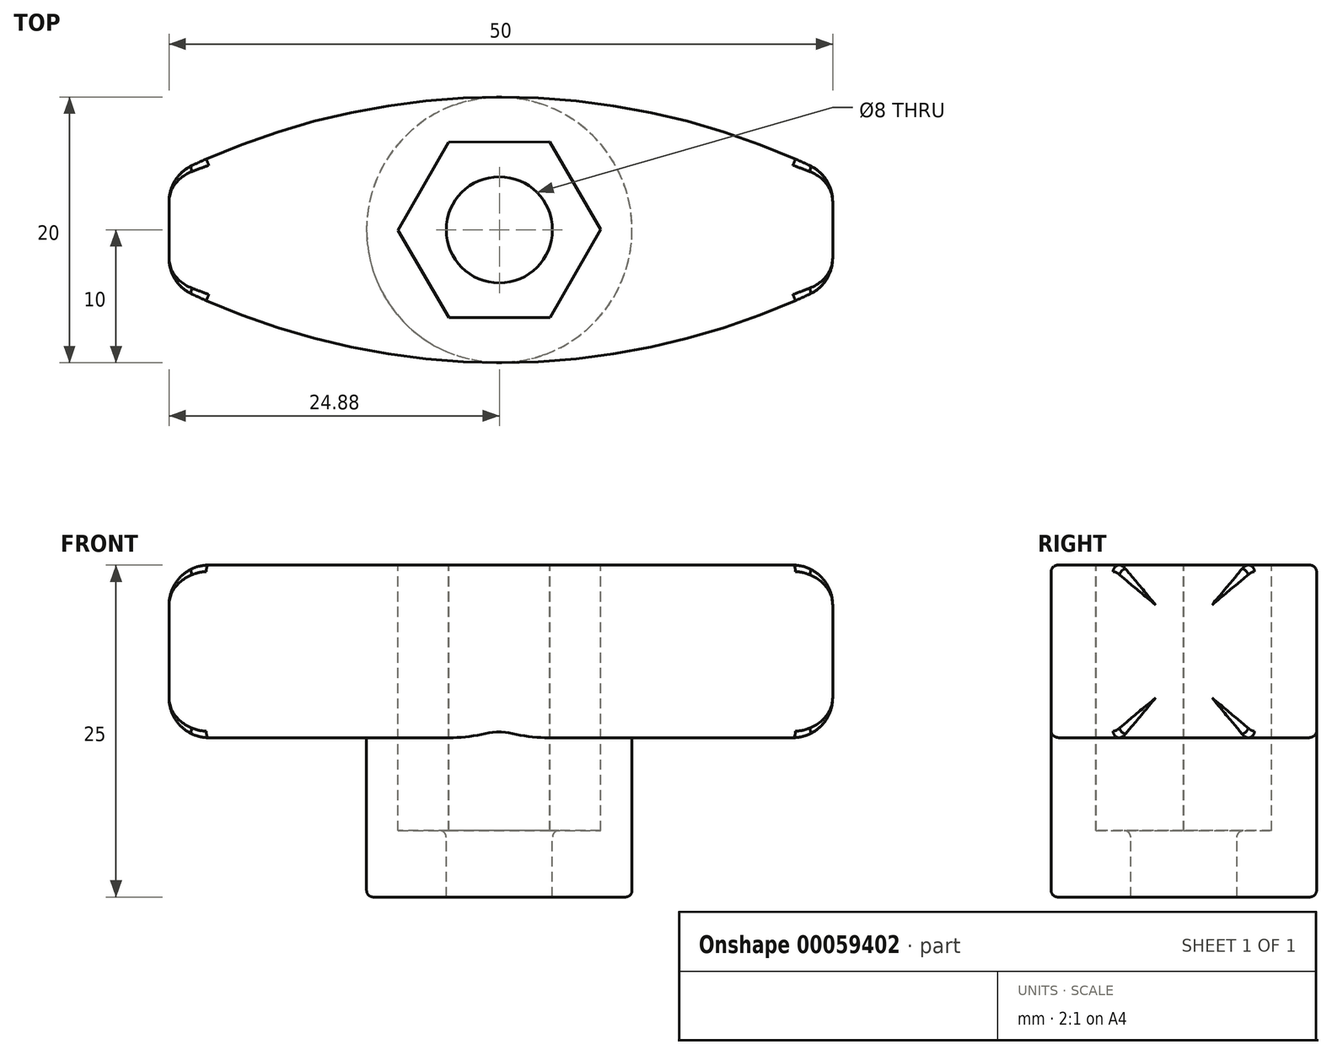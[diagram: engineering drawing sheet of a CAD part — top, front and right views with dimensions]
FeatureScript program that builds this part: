
annotation { "Feature Type Name" : "Feature", "Feature Type Description" : "" }
export const myFeature = defineFeature(function(context is Context, id is Id, definition is map)
    precondition{}
    {
        {
            var Q0;
            Q0=qCreatedBy(makeId("Top.planeOp"),FACE);
            var sketch = newSketch(context, id + "F0", { "sketchPlane" : qUnion([Q0])});
            skArc(sketch, "E0", {"start": v(25.12, 4) * mm, "mid": v(0.12, 10) * mm, "end": v(-24.88, 4) * mm});
            skArc(sketch, "E1.MirrorCS", {"start": v(25.12, -4) * mm, "mid": v(0.12, -10) * mm, "end": v(-24.88, -4) * mm});
            skLineSegment(sketch, "E2", {"start": v(-24.88, -4) * mm, "end": v(-24.88, 4) * mm});
            skLineSegment(sketch, "E3", {"start": v(25.12, 4) * mm, "end": v(25.12, -4) * mm});
            skSolve(sketch);
        }
        {
            var Q0;
            Q0 = qSketchRegion(id + "F0", true);
            extrude(context, id + "F1", {"entities" : qUnion([Q0]), "depth" : 13 * mm});
        }
        {
            var Q0;
            Q0=makeQuery(id+"F1.opExtrude","CAP_FACE",FACE,{"disambiguationData":[OSD([sQuery(id+"F0.wireOp",EDGE,"E0"),sQuery(id+"F0.wireOp",EDGE,"E1.MirrorCS"),sQuery(id+"F0.wireOp",EDGE,"E2"),sQuery(id+"F0.wireOp",EDGE,"E3")])],"isStart":true});
            var sketch = newSketch(context, id + "F2", { "sketchPlane" : qUnion([Q0])});
            skCircle(sketch, "E4", {"center": v(0, 0) * mm, "radius": 10 * mm});
            skSolve(sketch);
        }
        {
            var Q0;
            Q0 = qSketchRegion(id + "F2", true);
            extrude(context, id + "F3", {"entities" : qUnion([Q0]), "operationType" : NewBodyOperationType.ADD, "depth" : 12 * mm});
        }
        {
            var Q0;
            Q0=makeQuery(id+"F1.opExtrude","CAP_FACE",FACE,{"disambiguationData":[OSD([sQuery(id+"F0.wireOp",EDGE,"E0"),sQuery(id+"F0.wireOp",EDGE,"E1.MirrorCS"),sQuery(id+"F0.wireOp",EDGE,"E2"),sQuery(id+"F0.wireOp",EDGE,"E3")])],"isStart":false});
            var sketch = newSketch(context, id + "F4", { "sketchPlane" : qUnion([Q0])});
            skCircle(sketch, "E5", {"center": v(0, 0) * mm, "radius": 4 * mm});
            skSolve(sketch);
        }
        {
            var Q0;
            Q0=makeQuery(id+"F4.imprint","IMPRINT",FACE,{"disambiguationData":[TD([[makeQuery(id+"F4.imprint","IMPRINT",EDGE,{"derivedFrom":sQuery(id+"F4.wireOp",EDGE,"E5")}),1.0]])]});
            extrude(context, id + "F5", {"entities" : qUnion([Q0]), "operationType" : NewBodyOperationType.REMOVE, "oppositeDirection" : true, "depth" : 25 * mm});
        }
        {
            var Q0;
            Q0=makeQuery(id+"F1.opExtrude","CAP_FACE",FACE,{"disambiguationData":[OSD([sQuery(id+"F0.wireOp",EDGE,"E0"),sQuery(id+"F0.wireOp",EDGE,"E1.MirrorCS"),sQuery(id+"F0.wireOp",EDGE,"E2"),sQuery(id+"F0.wireOp",EDGE,"E3")])],"isStart":false});
            var sketch = newSketch(context, id + "F6", { "sketchPlane" : qUnion([Q0])});
            skCircle(sketch, "E6.cCircle", {"center": v(0, 0) * mm, "radius": 6.61 * mm, "construction": true});
            skLineSegment(sketch, "E6.0", {"start": v(-7.63, -0.02) * mm, "end": v(-3.83, 6.6) * mm});
            skLineSegment(sketch, "E6.1", {"start": v(-3.83, 6.6) * mm, "end": v(3.8, 6.62) * mm});
            skLineSegment(sketch, "E6.2", {"start": v(3.8, 6.62) * mm, "end": v(7.63, 0.02) * mm});
            skLineSegment(sketch, "E6.3", {"start": v(7.63, 0.02) * mm, "end": v(3.83, -6.6) * mm});
            skLineSegment(sketch, "E6.4", {"start": v(3.83, -6.6) * mm, "end": v(-3.8, -6.62) * mm});
            skLineSegment(sketch, "E6.5", {"start": v(-3.8, -6.62) * mm, "end": v(-7.63, -0.02) * mm});
            skPoint(sketch, "E6.0.midPoint", {"position": v(-5.73, 3.3) * mm});
            skSolve(sketch);
        }
        {
            var Q0;
            Q0 = qSketchRegion(id + "F6", true);
            extrude(context, id + "F7", {"entities" : qUnion([Q0]), "operationType" : NewBodyOperationType.REMOVE, "oppositeDirection" : true, "depth" : 20 * mm});
        }
        {
            var Q0;
            Q0=makeQuery(id+"F3.opExtrude","CAP_EDGE",EDGE,{"disambiguationData":[OSD([sQuery(id+"F2.wireOp",EDGE,"E4")])],"isStart":false});
            var Q1;
            Q1=makeQuery(id+"F5.boolean.opBoolean","COPY",EDGE,{"derivedFrom":makeQuery(id+"F5.opExtrude","CAP_EDGE",EDGE,{"disambiguationData":[OSD([sQuery(id+"F4.wireOp",EDGE,"E5")])],"isStart":false})});
            var Q2;
            Q2=makeQuery(id+"F7.boolean.opBoolean","INTERSECT",EDGE,{"derivedFrom":[makeQuery(id+"F5.boolean.opBoolean","COPY",FACE,{"derivedFrom":makeQuery(id+"F5.opExtrude","SWEPT_FACE",FACE,{"disambiguationData":[OSD([sQuery(id+"F4.wireOp",EDGE,"E5")])]})}),makeQuery(id+"F7.opExtrude","CAP_FACE",FACE,{"disambiguationData":[OSD([sQuery(id+"F6.wireOp",EDGE,"E6.0"),sQuery(id+"F6.wireOp",EDGE,"E6.1"),sQuery(id+"F6.wireOp",EDGE,"E6.2"),sQuery(id+"F6.wireOp",EDGE,"E6.3"),sQuery(id+"F6.wireOp",EDGE,"E6.4"),sQuery(id+"F6.wireOp",EDGE,"E6.5")])],"isStart":false})]});
            var Q3;
            Q3=makeQuery(id+"F7.boolean.opBoolean","COPY",EDGE,{"derivedFrom":makeQuery(id+"F7.opExtrude","CAP_EDGE",EDGE,{"disambiguationData":[OSD([sQuery(id+"F6.wireOp",EDGE,"E6.0")])],"isStart":true})});
            var Q4;
            Q4=makeQuery(id+"F7.boolean.opBoolean","COPY",EDGE,{"derivedFrom":makeQuery(id+"F7.opExtrude","CAP_EDGE",EDGE,{"disambiguationData":[OSD([sQuery(id+"F6.wireOp",EDGE,"E6.1")])],"isStart":true})});
            var Q5;
            Q5=makeQuery(id+"F7.boolean.opBoolean","COPY",EDGE,{"derivedFrom":makeQuery(id+"F7.opExtrude","CAP_EDGE",EDGE,{"disambiguationData":[OSD([sQuery(id+"F6.wireOp",EDGE,"E6.2")])],"isStart":true})});
            var Q6;
            Q6=makeQuery(id+"F7.boolean.opBoolean","COPY",EDGE,{"derivedFrom":makeQuery(id+"F7.opExtrude","CAP_EDGE",EDGE,{"disambiguationData":[OSD([sQuery(id+"F6.wireOp",EDGE,"E6.3")])],"isStart":true})});
            var Q7;
            Q7=makeQuery(id+"F7.boolean.opBoolean","COPY",EDGE,{"derivedFrom":makeQuery(id+"F7.opExtrude","CAP_EDGE",EDGE,{"disambiguationData":[OSD([sQuery(id+"F6.wireOp",EDGE,"E6.4")])],"isStart":true})});
            var Q8;
            Q8=makeQuery(id+"F7.boolean.opBoolean","COPY",EDGE,{"derivedFrom":makeQuery(id+"F7.opExtrude","CAP_EDGE",EDGE,{"disambiguationData":[OSD([sQuery(id+"F6.wireOp",EDGE,"E6.5")])],"isStart":true})});
            var Q9;
            Q9=makeQuery(id+"F1.opExtrude","CAP_EDGE",EDGE,{"disambiguationData":[OSD([sQuery(id+"F0.wireOp",EDGE,"E0")])],"isStart":false});
            var Q10;
            Q10=makeQuery(id+"F1.opExtrude","CAP_EDGE",EDGE,{"disambiguationData":[OSD([sQuery(id+"F0.wireOp",EDGE,"E1.MirrorCS")])],"isStart":false});
            var Q11;
            {var subQ0=sQuery(id+"F0.wireOp",EDGE,"E0");var subQ1=sQuery(id+"F0.wireOp",EDGE,"E3");Q11=makeQuery(id+"F3.boolean.opBoolean","SPLIT",EDGE,{"disambiguationData":[TD([makeQuery(id+"F1.opExtrude","SWEPT_FACE",FACE,{"disambiguationData":[OSD([subQ1])]})])],"derivedFrom":makeQuery(id+"F1.opExtrude","CAP_EDGE",EDGE,{"disambiguationData":[OSD([subQ0])],"isStart":true})});}
            var Q12;
            {var subQ0=sQuery(id+"F0.wireOp",EDGE,"E3");var subQ1=sQuery(id+"F0.wireOp",EDGE,"E1.MirrorCS");Q12=makeQuery(id+"F3.boolean.opBoolean","SPLIT",EDGE,{"disambiguationData":[TD([makeQuery(id+"F1.opExtrude","SWEPT_FACE",FACE,{"disambiguationData":[OSD([subQ0])]})])],"derivedFrom":makeQuery(id+"F1.opExtrude","CAP_EDGE",EDGE,{"disambiguationData":[OSD([subQ1])],"isStart":true})});}
            fillet(context, id + "F8", {"entities" : qUnion([Q0, Q1, Q2, Q3, Q4, Q5, Q6, Q7, Q8, Q9, Q10, Q11, Q12]), "radius" : .5 * mm, "tangentPropagation" : true, "allowEdgeOverflow" : false});
        }
        {
            var Q0;
            Q0=makeQuery(id+"F1.opExtrude","CAP_EDGE",EDGE,{"disambiguationData":[OSD([sQuery(id+"F0.wireOp",EDGE,"E3")])],"isStart":true});
            var Q1;
            Q1=makeQuery(id+"F1.opExtrude","SWEPT_EDGE",EDGE,{"disambiguationData":[OSD([sQuery(id+"F0.wireOp",EDGE,"E1.MirrorCS"),sQuery(id+"F0.wireOp",EDGE,"E2")])]});
            fillet(context, id + "F9", {"entities" : qUnion([Q0, Q1]), "radius" : 3 * mm, "tangentPropagation" : true, "allowEdgeOverflow" : false});
        }
    });
